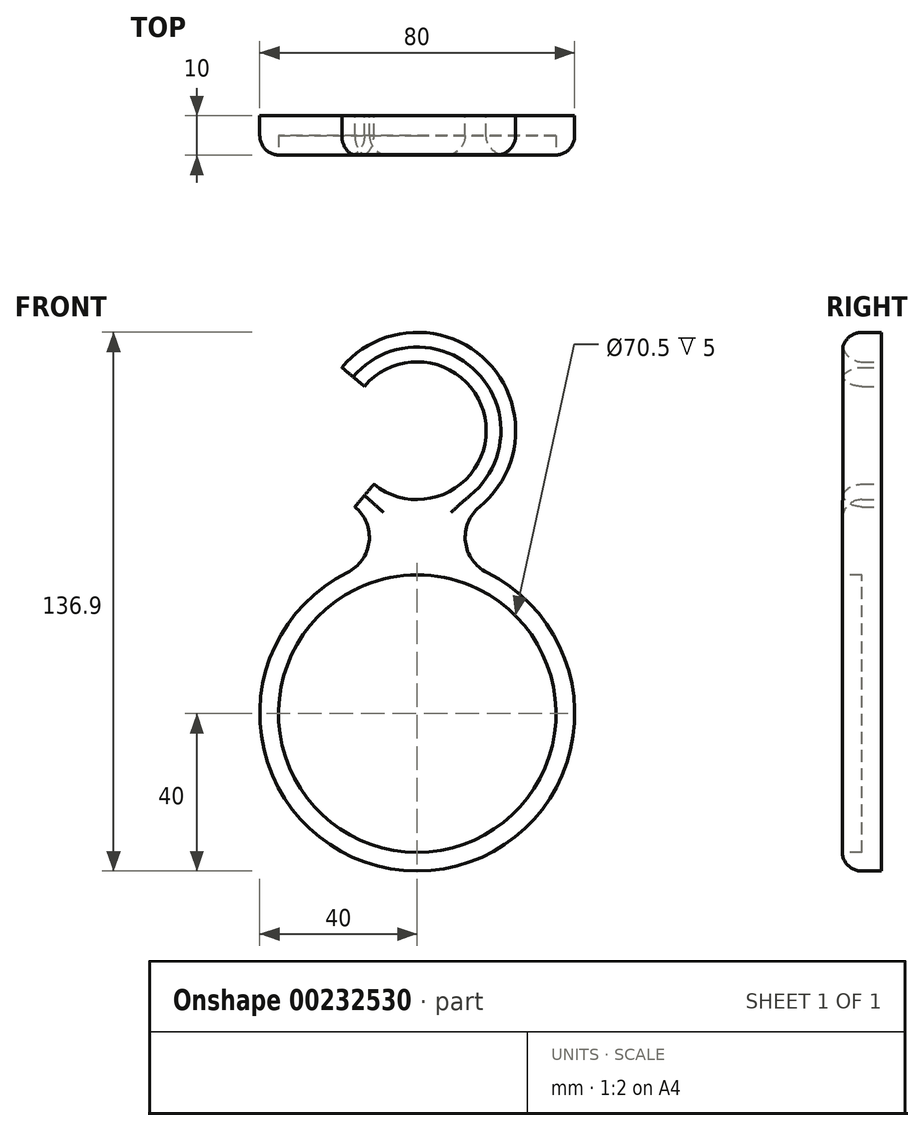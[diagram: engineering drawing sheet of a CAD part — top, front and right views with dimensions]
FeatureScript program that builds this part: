
annotation { "Feature Type Name" : "Feature", "Feature Type Description" : "" }
export const myFeature = defineFeature(function(context is Context, id is Id, definition is map)
    precondition{}
    {
        {
            var Q0;
            Q0=qCreatedBy(makeId("Front.planeOp"),FACE);
            var sketch = newSketch(context, id + "F0", { "sketchPlane" : qUnion([Q0])});
            skArc(sketch, "E0", {"start": v(-17.74, 35.85) * mm, "mid": v(0, -40) * mm, "end": v(17.74, 35.85) * mm});
            skArc(sketch, "E1", {"start": v(15.84, 52.55) * mm, "mid": v(17.78, 89.47) * mm, "end": v(-19.15, 87.97) * mm});
            skArc(sketch, "E2", {"start": v(-11.02, 58.3) * mm, "mid": v(17.42, 73.57) * mm, "end": v(-13.4, 83.14) * mm});
            skLineSegment(sketch, "E3", {"start": v(-13.4, 83.14) * mm, "end": v(-19.15, 87.97) * mm});
            skLineSegment(sketch, "E4", {"start": v(0, 71.9) * mm, "end": v(-90.58, 71.9) * mm, "construction": true});
            skArc(sketch, "E5", {"start": v(-17.74, 35.85) * mm, "mid": v(-12.24, 43.68) * mm, "end": v(-15.84, 52.55) * mm});
            skArc(sketch, "E6", {"start": v(15.84, 52.55) * mm, "mid": v(12.24, 43.68) * mm, "end": v(17.74, 35.85) * mm});
            skLineSegment(sketch, "E7", {"start": v(-11.02, 58.3) * mm, "end": v(-15.84, 52.55) * mm});
            skSolve(sketch);
        }
        {
            var Q0;
            Q0 = qSketchRegion(id + "F0", true);
            extrude(context, id + "F1", {"entities" : qUnion([Q0]), "depth" : 10 * mm});
        }
        {
            var Q0;
            Q0=makeQuery(id+"F1.opExtrude","CAP_FACE",FACE,{"disambiguationData":[OSD([sQuery(id+"F0.wireOp",EDGE,"E0"),sQuery(id+"F0.wireOp",EDGE,"E1"),sQuery(id+"F0.wireOp",EDGE,"E2"),sQuery(id+"F0.wireOp",EDGE,"E3"),sQuery(id+"F0.wireOp",EDGE,"E5"),sQuery(id+"F0.wireOp",EDGE,"E6"),sQuery(id+"F0.wireOp",EDGE,"E7")])],"isStart":false});
            var sketch = newSketch(context, id + "F2", { "sketchPlane" : qUnion([Q0])});
            skCircle(sketch, "E8", {"center": v(0, 0) * mm, "radius": 35.25 * mm});
            skSolve(sketch);
        }
        {
            var Q0;
            Q0 = qSketchRegion(id + "F2", true);
            extrude(context, id + "F3", {"entities" : qUnion([Q0]), "operationType" : NewBodyOperationType.REMOVE, "oppositeDirection" : true, "depth" : 5 * mm});
        }
        {
            var Q0;
            Q0=makeQuery(id+"F1.opExtrude","CAP_EDGE",EDGE,{"disambiguationData":[OSD([sQuery(id+"F0.wireOp",EDGE,"E1")])],"isStart":false});
            var Q1;
            Q1=makeQuery(id+"F1.opExtrude","CAP_EDGE",EDGE,{"disambiguationData":[OSD([sQuery(id+"F0.wireOp",EDGE,"E2")])],"isStart":false});
            var Q2;
            Q2=makeQuery(id+"F1.opExtrude","CAP_EDGE",EDGE,{"disambiguationData":[OSD([sQuery(id+"F0.wireOp",EDGE,"E3")])],"isStart":false});
            var Q3;
            Q3=makeQuery(id+"F1.opExtrude","CAP_EDGE",EDGE,{"disambiguationData":[OSD([sQuery(id+"F0.wireOp",EDGE,"E7")])],"isStart":false});
            fillet(context, id + "F4", {"entities" : qUnion([Q0, Q1, Q2, Q3]), "radius" : 5 * mm, "tangentPropagation" : true, "allowEdgeOverflow" : false});
        }
    });
